# Revit family: CENTUM Einfachanschlüss stehend
name_source: partatom
category: HLS-Bauteile
revit_build: Autodesk Revit 2017 (Build: 20190507_1515(x64)
units: mm (PartAtom-declared; Revit-internal decimal feet)

## family parameters
Arbeitsebenenbasiert = Ja
Beim Laden mit Abzugskörper schneiden = Nein
Bemaßung runder Anschluss = Durchmesser verwenden
Gemeinsam genutzt = Ja
Immer vertikal = Nein
Raumberechnungspunkt = Nein
Teiletyp = Normal

## types (11) — shared parameters
Anzahl Befestigungsloch = 2 St
Fabrikat = MEFA
Firma = MEFA Befestigungs- und Montagesysteme GmbH
H2 = 19 mm  [stored 0.062336 ft]
Langloch = 14x40 mm
Länge = 70 mm  [stored 0.229659 ft]
MD = 4 mm  [stored 0.0131234 ft]
Material = Stahl
Materialname = S235
Mengeneinheit = St
Oberflaeche = Zink-Nickel
Sicherheitsfaktor = 1.54
Stärke = 4 mm  [stored 0.0131234 ft]
Vorgabe-Ansicht = 1219 mm
vpe = 1 St
zero-valued in all types: Höhe Anschlussplatte

## per-type parameters (varying)
| type | Anschluss | Anschlussgewinde | Artikelnummer | B | Breite | EAN | Gewicht | Gewicht pro Bauteil | H | H1 | HGA | Höhe | Höhe bis Lochung | Kurztext1 | Kurztext2 | Profiltyp | max. zul. Last |
| CENTUM Einfachanschluss XL 80, M16 | M16 | 6kt-Mutter parametrik : Mutter M16 (4120522) | 1640818007 | 81 mm  [stored 0.265748 ft] | 82 mm  [stored 0.269029 ft] | 4250928458445 | 0.48 kg | 0.48 kg | 64 mm | 41 mm | 15 mm  [stored 0.0492126 ft] | 64 mm | 40 mm | Einfachanschluss M16 | für Profiltyp XL 80 | XL 80 | 4.00 kN |
| CENTUM Einfachanschluss XL100/ XL200, M16 | M16 | 6kt-Mutter parametrik : Mutter M16 (4120522) | 1641018007 | 101 mm  [stored 0.331365 ft] | 110 mm  [stored 0.360892 ft] | 4250928437068 | 0.56 kg | 0.56 kg | 74 mm | 51 mm | 15 mm  [stored 0.0492126 ft] | 74 mm | 50 mm | Einfachanschluss M16 | für Profiltyp XL 100, XL 200 | XL 100, XL 200 | 5.00 kN |
| CENTUM Einfachanschluss XL120, M16 | M16 | 6kt-Mutter parametrik : Mutter M16 (4120522) | 1641218007 | 101 mm  [stored 0.331365 ft] | 130 mm  [stored 0.426509 ft] | 4250928437136 | 0.62 kg | 0.62 kg | 84 mm  [stored 0.275591 ft] | 61 mm  [stored 0.200131 ft] | 15 mm  [stored 0.0492126 ft] | 84 mm | 60 mm | Einfachanschluss M16 | für Profiltyp XL 120 | XL 120 | 5.00 kN |
| CENTUM Einfachanschluss XL 80, 1/2" | 1/2'' | Runde Gewindeanschlusse parametrik : Muffe 1/2´´ (0009865) | 1640818008 | 81 mm  [stored 0.265748 ft] | 82 mm  [stored 0.269029 ft] | 4250928458452 | 0.47 kg | 0.47 kg | 64 mm | 41 mm | 15 mm  [stored 0.0492126 ft] | 64 mm | 40 mm | Einfachanschluss 1/2" | für Profiltyp XL 80 | XL 80 | 4.00 kN |
| CENTUM Einfachanschluss XL100/ XL200, M12 | M12 | 6kt-Mutter parametrik : Mutter M12 (4120484) | 1641018006 | 101 mm  [stored 0.331365 ft] | 110 mm  [stored 0.360892 ft] | 4250928437051 | 0.55 kg | 0.55 kg | 74 mm | 51 mm | 8 mm  [stored 0.0262467 ft] | 74 mm | 50 mm | Einfachanschluss M12 | für Profiltyp XL 100, XL 200 | XL 100, XL 200 | 5.00 kN |
| CENTUM Einfachanschluss XL100/ XL200, 1/2" | 1/2'' | Runde Gewindeanschlusse parametrik : Muffe 1/2´´ (0009865) | 1641018008 | 101 mm  [stored 0.331365 ft] | 110 mm  [stored 0.360892 ft] | 4250928437075 | 0.56 kg | 0.56 kg | 74 mm | 51 mm | 15 mm  [stored 0.0492126 ft] | 74 mm | 50 mm | Einfachanschluss 1/2" | für Profiltyp XL 100, XL 200 | XL 100, XL 200 | 5.00 kN |
| CENTUM Einfachanschluss XL100/ XL200, 1" | 1'' | Runde Gewindeanschlusse parametrik : Muffe 1´´ (0009881) | 1641018010 | 101 mm  [stored 0.331365 ft] | 110 mm  [stored 0.360892 ft] | 4250928437082 | 0.61 kg | 0.61 kg | 74 mm | 51 mm | 20 mm  [stored 0.0656168 ft] | 74 mm | 50 mm | Einfachanschluss 1" | für Profiltyp XL 100, XL 200 | XL 100, XL 200 | 5.00 kN |
| CENTUM Einfachanschluss XL120, 1/2" | 1/2'' | Runde Gewindeanschlusse parametrik : Muffe 1/2´´ (0009865) | 1641218008 | 101 mm  [stored 0.331365 ft] | 130 mm  [stored 0.426509 ft] | 4250928437143 | 0.61 kg | 0.61 kg | 84 mm  [stored 0.275591 ft] | 61 mm  [stored 0.200131 ft] | 15 mm  [stored 0.0492126 ft] | 84 mm | 60 mm | Einfachanschluss 1/2" | für Profiltyp XL 120 | XL 120 | 5.00 kN |
| CENTUM Einfachanschluss XL120, 1" | 1'' | Runde Gewindeanschlusse parametrik : Muffe 1´´ (0009881) | 1641218010 | 101 mm  [stored 0.331365 ft] | 130 mm  [stored 0.426509 ft] | 4250928437150 | 0.66 kg | 0.66 kg | 84 mm  [stored 0.275591 ft] | 61 mm  [stored 0.200131 ft] | 20 mm  [stored 0.0656168 ft] | 84 mm | 60 mm | Einfachanschluss 1" | für Profiltyp XL 120 | XL 120 | 5.00 kN |
| CENTUM Einfachanschluss XL 80, 1" | 1'' | Runde Gewindeanschlusse parametrik : Muffe 1´´ (0009881) | 1640818010 | 81 mm  [stored 0.265748 ft] | 82 mm  [stored 0.269029 ft] | 4250928458469 | 0.52 kg | 0.52 kg | 64 mm | 41 mm | 20 mm  [stored 0.0656168 ft] | 64 mm | 40 mm | Einfachanschluss 1" | für Profiltyp XL 80 | XL 80 | 4.00 kN |
| CENTUM Einfachanschluss XL100/ XL200, 3/4" | 1'' | Runde Gewindeanschlusse parametrik : Muffe 1´´ (0009881) | 1641018009 | 101 mm  [stored 0.331365 ft] | 110 mm  [stored 0.360892 ft] |  | 0.00 kg | 0.00 kg | 74 mm | 51 mm | 20 mm  [stored 0.0656168 ft] | 74 mm | 50 mm |  | für Profiltyp XL 100, XL 200 | XL 100, XL 200 | 5.00 kN |

note: [stored X ft] marks values corroborated as IEEE doubles in the binary element streams (Revit-internal decimal feet)

## geometry (parser evidence)
native form markers: Sweep x4
no freeform markers — native parametric forms only
